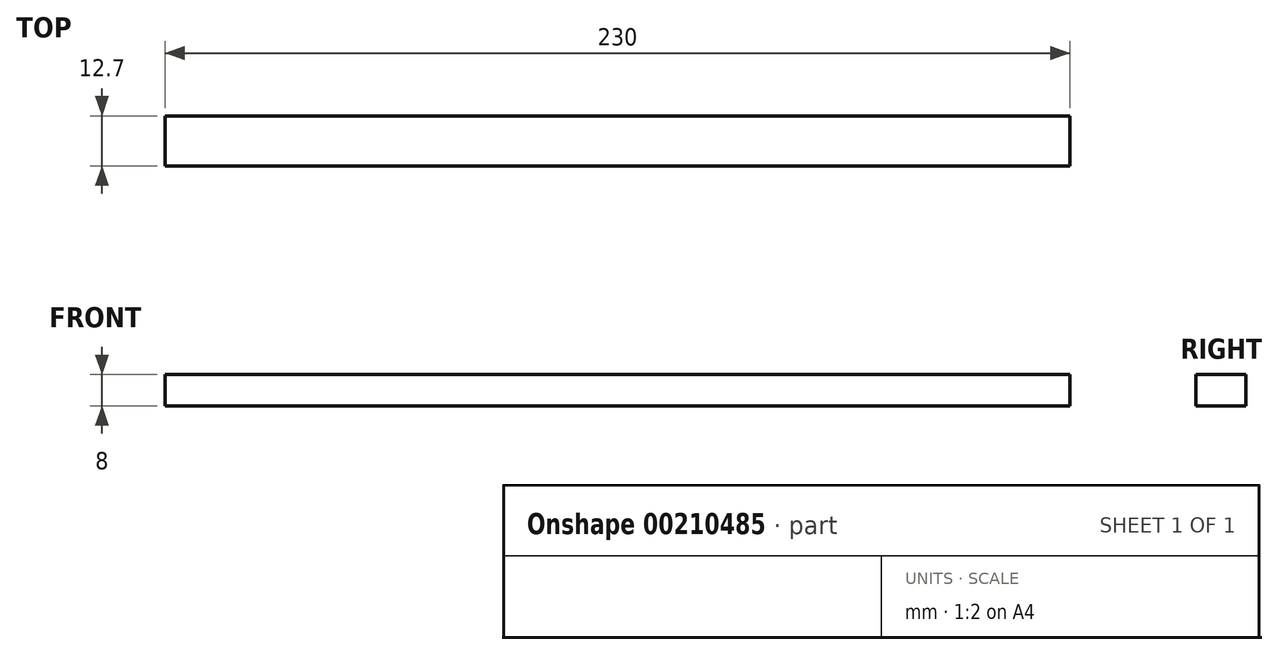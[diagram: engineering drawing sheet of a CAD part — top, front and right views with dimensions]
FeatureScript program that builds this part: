
annotation { "Feature Type Name" : "Feature", "Feature Type Description" : "" }
export const myFeature = defineFeature(function(context is Context, id is Id, definition is map)
    precondition{}
    {
        {
            var Q0;
            Q0=qCreatedBy(makeId("Top.planeOp"),FACE);
            var sketch = newSketch(context, id + "F0", { "sketchPlane" : qUnion([Q0])});
            skLineSegment(sketch, "E0.bottom", {"start": v(0, 0) * mm, "end": v(230, 0) * mm});
            skLineSegment(sketch, "E0.top", {"start": v(0, 12.7) * mm, "end": v(230, 12.7) * mm});
            skLineSegment(sketch, "E0.left", {"start": v(0, 0) * mm, "end": v(0, 12.7) * mm});
            skLineSegment(sketch, "E0.right", {"start": v(230, 0) * mm, "end": v(230, 12.7) * mm});
            skSolve(sketch);
        }
        {
            var Q0;
            Q0 = qSketchRegion(id + "F0", true);
            extrude(context, id + "F1", {"entities" : qUnion([Q0]), "depth" : 8 * mm});
        }
    });
